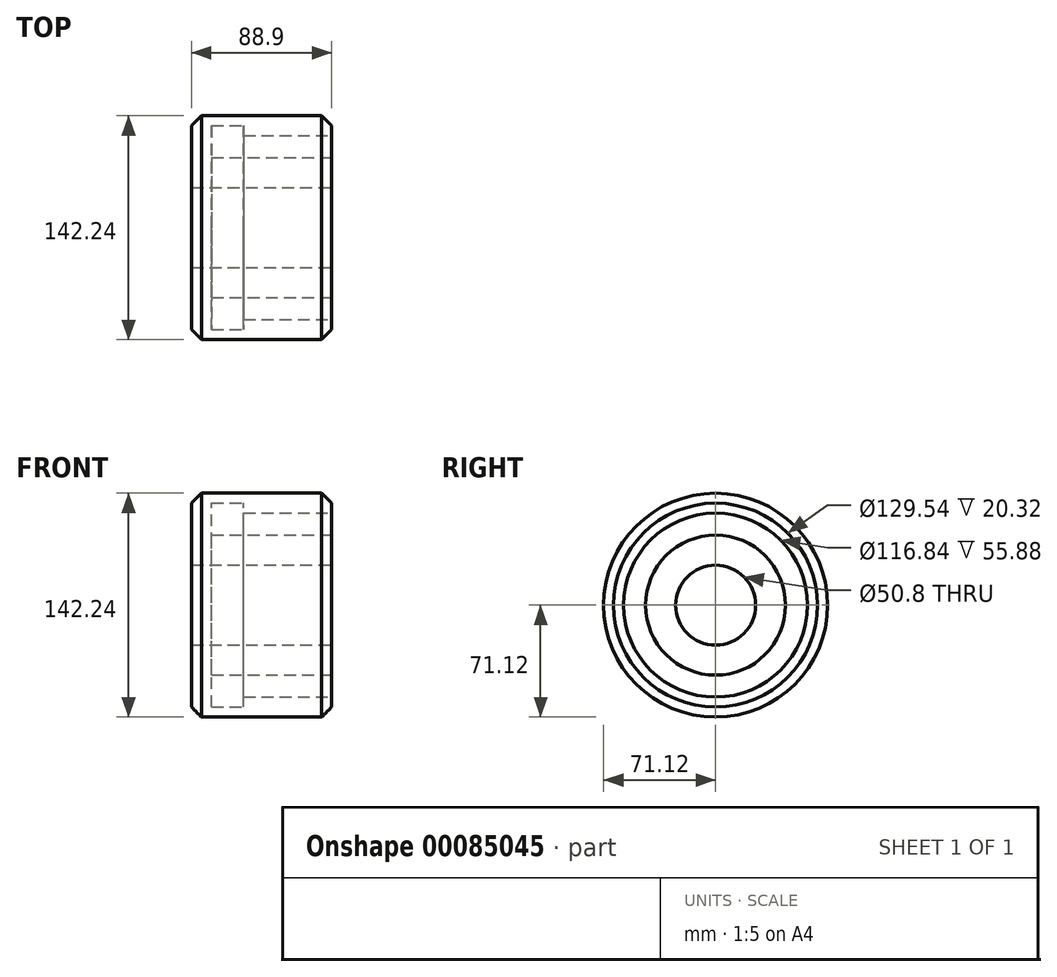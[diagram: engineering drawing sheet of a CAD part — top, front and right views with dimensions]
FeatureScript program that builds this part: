
annotation { "Feature Type Name" : "Feature", "Feature Type Description" : "" }
export const myFeature = defineFeature(function(context is Context, id is Id, definition is map)
    precondition{}
    {
        {
            var Q0;
            Q0=qCreatedBy(makeId("Front.planeOp"),FACE);
            var sketch = newSketch(context, id + "F0", { "sketchPlane" : qUnion([Q0])});
            skLineSegment(sketch, "E0", {"start": v(57.21, 0) * mm, "end": v(-64.7, 0) * mm, "construction": true});
            skLineSegment(sketch, "E1.bottom", {"start": v(41.24, 25.4) * mm, "end": v(-47.66, 25.4) * mm});
            skLineSegment(sketch, "E1.top", {"start": v(41.24, 71.12) * mm, "end": v(-47.66, 71.12) * mm});
            skLineSegment(sketch, "E1.left", {"start": v(41.24, 25.4) * mm, "end": v(41.24, 44.45) * mm});
            skLineSegment(sketch, "E1.right", {"start": v(-47.66, 25.4) * mm, "end": v(-47.66, 71.12) * mm});
            skLineSegment(sketch, "E2", {"start": v(41.24, 58.42) * mm, "end": v(-14.64, 58.42) * mm});
            skLineSegment(sketch, "E3", {"start": v(-14.64, 58.42) * mm, "end": v(-14.64, 64.77) * mm});
            skLineSegment(sketch, "E4", {"start": v(-14.64, 64.77) * mm, "end": v(-34.96, 64.77) * mm});
            skLineSegment(sketch, "E5", {"start": v(-34.96, 64.77) * mm, "end": v(-34.96, 44.45) * mm});
            skLineSegment(sketch, "E6", {"start": v(-34.96, 44.45) * mm, "end": v(41.24, 44.45) * mm});
            skLineSegment(sketch, "E7.trimOffspring", {"start": v(41.24, 58.42) * mm, "end": v(41.24, 71.12) * mm});
            skSolve(sketch);
        }
        {
            var Q0;
            Q0=makeQuery(id+"F0.imprint","IMPRINT",FACE,{"disambiguationData":[TD([[makeQuery(id+"F0.imprint","IMPRINT",EDGE,{"derivedFrom":sQuery(id+"F0.wireOp",EDGE,"E1.bottom")}),-1.0]])]});
            var Q1;
            Q1=sQuery(id+"F0.wireOp",EDGE,"E0");
            revolve(context, id + "F1", {"entities" : qUnion([Q0]), "axis" : qUnion([Q1]), "revolveType" : RevolveType.FULL});
        }
        {
            var Q0;
            Q0=makeQuery(id+"F1.opRevolve","SWEPT_EDGE",EDGE,{"disambiguationData":[OSD([sQuery(id+"F0.wireOp",EDGE,"E1.top"),sQuery(id+"F0.wireOp",EDGE,"E7.trimOffspring")])]});
            var Q1;
            Q1=makeQuery(id+"F1.opRevolve","SWEPT_EDGE",EDGE,{"disambiguationData":[OSD([sQuery(id+"F0.wireOp",EDGE,"E1.top"),sQuery(id+"F0.wireOp",EDGE,"E1.right")])]});
            chamfer(context, id + "F2", {"entities" : qUnion([Q0, Q1]), "width" : 6.35 * mm, "tangentPropagation" : true});
        }
    });
